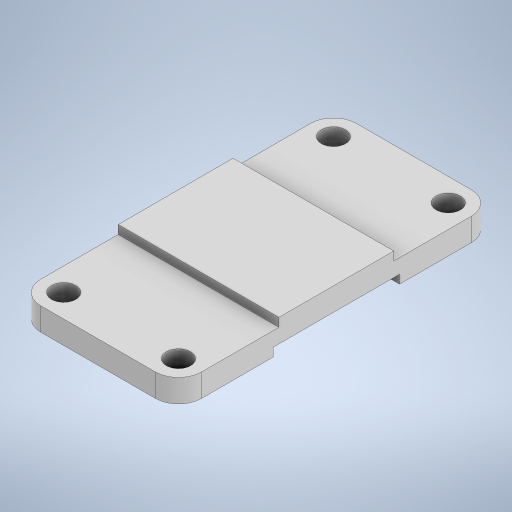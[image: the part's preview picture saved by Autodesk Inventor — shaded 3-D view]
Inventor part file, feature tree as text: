
AUTODESK INVENTOR PART (.ipt)
format: ipt  version: 2024 (Build 280153000, 153)  size: 268,288 bytes
history: native  units: mm
features: extrude x3, sketch x2, other x1
ambient origin geometry x8: Origin, YZ Plane, XZ Plane, XY Plane, X Axis, Y Axis, Z Axis, Center Point
bodies: Body1 (feature_tree)
feature tree (6):
  other  "Sólido1"
  sketch  "Boceto1"  dims[d0=56.0mm d1=110.0mm]
  extrude  "Extrusión1"  Depth=110.0mm
  extrude  "Extrusión2"  Depth=3.0mm
  extrude  "Extrusión3"  Depth=3.0mm
  sketch  "Boceto2"  dims[d2=8.0mm d3=8.5mm d4=8.5mm d5=8.5mm d6=8.5mm d7=56.0mm d8=40.0mm d9=8.0mm d10=0.0mm d11=11.0mm d12=0.0mm d13=44.0mm d14=3.0mm d15=0.0mm d16=0.0mm]
